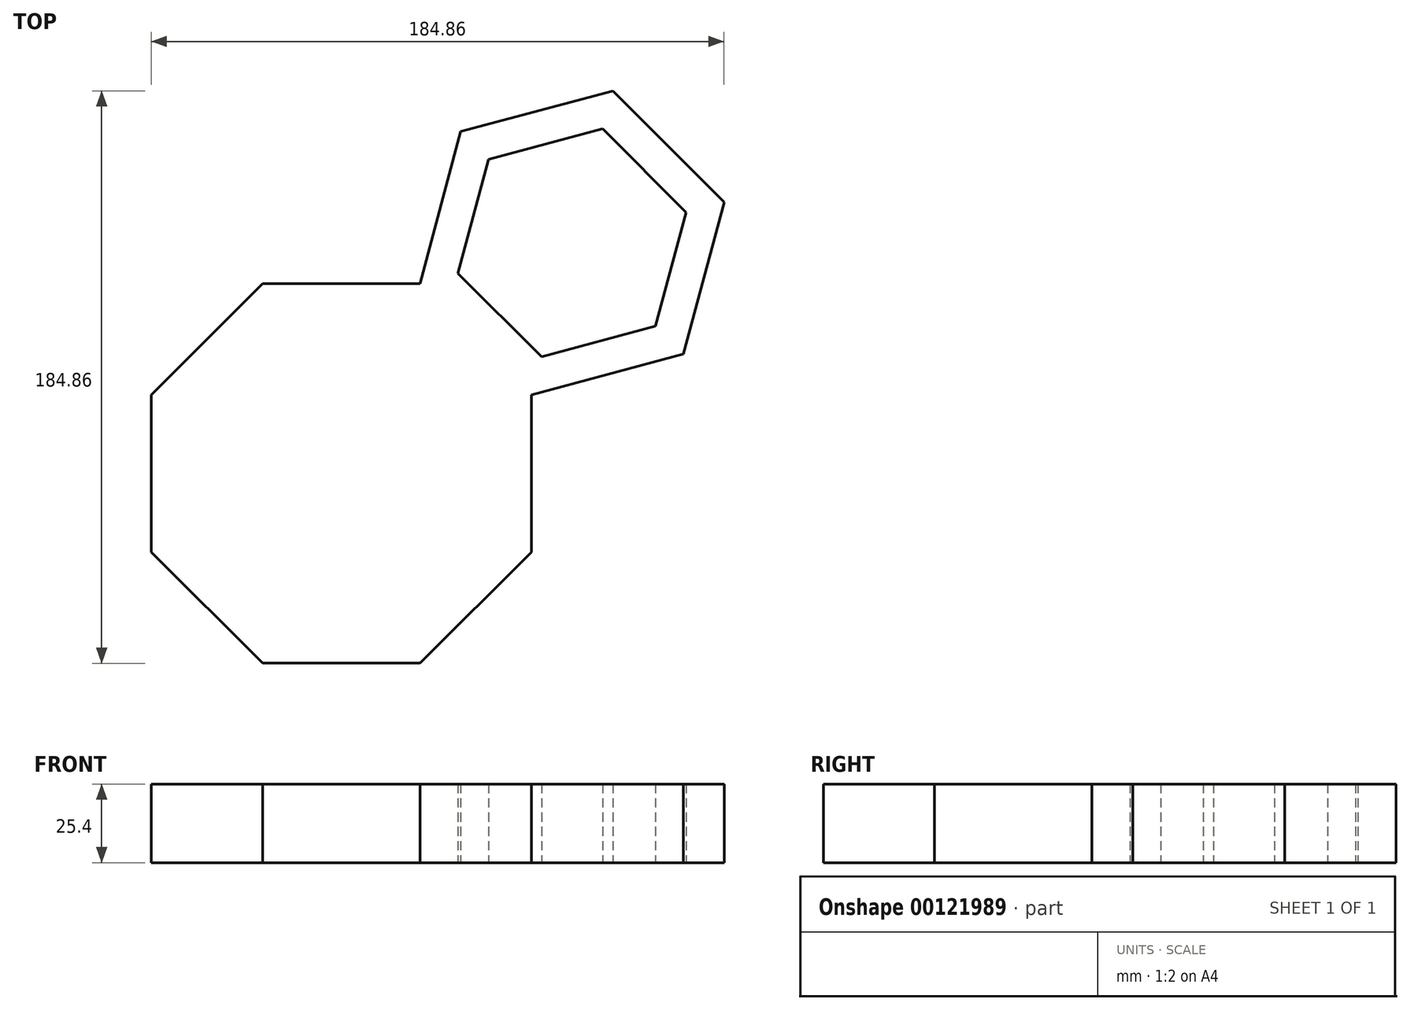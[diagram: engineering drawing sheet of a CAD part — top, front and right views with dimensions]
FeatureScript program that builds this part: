
annotation { "Feature Type Name" : "Feature", "Feature Type Description" : "" }
export const myFeature = defineFeature(function(context is Context, id is Id, definition is map)
    precondition{}
    {
        {
            var Q0;
            Q0=qCreatedBy(makeId("Top.planeOp"),FACE);
            var sketch = newSketch(context, id + "F0", { "sketchPlane" : qUnion([Q0])});
            skCircle(sketch, "E0.cCircle", {"center": v(-1.9, -3.87) * mm, "radius": 61.32 * mm, "construction": true});
            skLineSegment(sketch, "E0.0", {"start": v(59.43, 21.53) * mm, "end": v(59.43, -29.27) * mm});
            skLineSegment(sketch, "E0.1", {"start": v(59.43, -29.27) * mm, "end": v(23.5, -65.2) * mm});
            skLineSegment(sketch, "E0.2", {"start": v(23.5, -65.2) * mm, "end": v(-27.3, -65.2) * mm});
            skLineSegment(sketch, "E0.3", {"start": v(-27.3, -65.2) * mm, "end": v(-63.22, -29.27) * mm});
            skLineSegment(sketch, "E0.4", {"start": v(-63.22, -29.27) * mm, "end": v(-63.22, 21.53) * mm});
            skLineSegment(sketch, "E0.5", {"start": v(-63.22, 21.53) * mm, "end": v(-27.3, 57.45) * mm});
            skLineSegment(sketch, "E0.6", {"start": v(-27.3, 57.45) * mm, "end": v(23.5, 57.45) * mm});
            skLineSegment(sketch, "E0.7", {"start": v(23.5, 57.45) * mm, "end": v(59.43, 21.53) * mm});
            skPoint(sketch, "E0.0.midPoint", {"position": v(59.43, -3.87) * mm});
            skPoint(sketch, "E1.0.midPoint", {"position": v(19.57, 48.7) * mm});
            skCircle(sketch, "E2.cCircle", {"center": v(72.57, 70.6) * mm, "radius": 44 * mm, "construction": true});
            skLineSegment(sketch, "E2.0", {"start": v(36.65, 106.52) * mm, "end": v(85.72, 119.66) * mm});
            skLineSegment(sketch, "E2.1", {"start": v(85.72, 119.66) * mm, "end": v(121.64, 83.74) * mm});
            skLineSegment(sketch, "E2.2", {"start": v(121.64, 83.74) * mm, "end": v(108.5, 34.67) * mm});
            skLineSegment(sketch, "E2.3", {"start": v(108.5, 34.67) * mm, "end": v(59.43, 21.53) * mm});
            skLineSegment(sketch, "E2.4", {"start": v(59.43, 21.53) * mm, "end": v(23.5, 57.45) * mm});
            skLineSegment(sketch, "E2.5", {"start": v(23.5, 57.45) * mm, "end": v(36.65, 106.52) * mm});
            skPoint(sketch, "E2.0.midPoint", {"position": v(61.19, 113.09) * mm});
            skCircle(sketch, "E3.cCircle", {"center": v(72.57, 70.6) * mm, "radius": 33 * mm, "construction": true});
            skLineSegment(sketch, "E3.0", {"start": v(82.43, 107.4) * mm, "end": v(109.38, 80.46) * mm});
            skLineSegment(sketch, "E3.1", {"start": v(109.38, 80.46) * mm, "end": v(99.51, 43.65) * mm});
            skLineSegment(sketch, "E3.2", {"start": v(99.51, 43.65) * mm, "end": v(62.71, 33.8) * mm});
            skLineSegment(sketch, "E3.3", {"start": v(62.71, 33.8) * mm, "end": v(35.77, 60.73) * mm});
            skLineSegment(sketch, "E3.4", {"start": v(35.77, 60.73) * mm, "end": v(45.63, 97.54) * mm});
            skLineSegment(sketch, "E3.5", {"start": v(45.63, 97.54) * mm, "end": v(82.43, 107.4) * mm});
            skPoint(sketch, "E3.0.midPoint", {"position": v(95.9, 93.93) * mm});
            skCircle(sketch, "E4.cCircle", {"center": v(-76.36, 70.6) * mm, "radius": 44 * mm, "construction": true});
            skLineSegment(sketch, "E4.0", {"start": v(-27.3, 57.45) * mm, "end": v(-63.22, 21.53) * mm});
            skLineSegment(sketch, "E4.1", {"start": v(-63.22, 21.53) * mm, "end": v(-112.29, 34.67) * mm});
            skLineSegment(sketch, "E4.2", {"start": v(-112.29, 34.67) * mm, "end": v(-125.43, 83.74) * mm});
            skLineSegment(sketch, "E4.3", {"start": v(-125.43, 83.74) * mm, "end": v(-89.51, 119.66) * mm});
            skLineSegment(sketch, "E4.4", {"start": v(-89.51, 119.66) * mm, "end": v(-40.44, 106.52) * mm});
            skLineSegment(sketch, "E4.5", {"start": v(-40.44, 106.52) * mm, "end": v(-27.3, 57.45) * mm});
            skPoint(sketch, "E4.0.midPoint", {"position": v(-45.26, 39.49) * mm});
            skCircle(sketch, "E5.cCircle", {"center": v(-76.36, 70.6) * mm, "radius": 33 * mm, "construction": true});
            skLineSegment(sketch, "E5.0", {"start": v(-49.42, 97.54) * mm, "end": v(-39.56, 60.73) * mm});
            skLineSegment(sketch, "E5.1", {"start": v(-39.56, 60.73) * mm, "end": v(-66.5, 33.8) * mm});
            skLineSegment(sketch, "E5.2", {"start": v(-66.5, 33.8) * mm, "end": v(-103.3, 43.65) * mm});
            skLineSegment(sketch, "E5.3", {"start": v(-103.3, 43.65) * mm, "end": v(-113.17, 80.46) * mm});
            skLineSegment(sketch, "E5.4", {"start": v(-113.17, 80.46) * mm, "end": v(-86.23, 107.4) * mm});
            skLineSegment(sketch, "E5.5", {"start": v(-86.23, 107.4) * mm, "end": v(-49.42, 97.54) * mm});
            skPoint(sketch, "E5.0.midPoint", {"position": v(-44.5, 79.13) * mm});
            skCircle(sketch, "E6.cCircle", {"center": v(72.57, -78.34) * mm, "radius": 44 * mm, "construction": true});
            skLineSegment(sketch, "E6.0", {"start": v(23.5, -65.2) * mm, "end": v(59.43, -29.27) * mm});
            skLineSegment(sketch, "E6.1", {"start": v(59.43, -29.27) * mm, "end": v(108.5, -42.42) * mm});
            skLineSegment(sketch, "E6.2", {"start": v(108.5, -42.42) * mm, "end": v(121.64, -91.5) * mm});
            skLineSegment(sketch, "E6.3", {"start": v(121.64, -91.5) * mm, "end": v(85.72, -127.41) * mm});
            skLineSegment(sketch, "E6.4", {"start": v(85.72, -127.41) * mm, "end": v(36.65, -114.26) * mm});
            skLineSegment(sketch, "E6.5", {"start": v(36.65, -114.26) * mm, "end": v(23.5, -65.2) * mm});
            skPoint(sketch, "E6.0.midPoint", {"position": v(41.47, -47.23) * mm});
            skCircle(sketch, "E7.cCircle", {"center": v(72.57, -78.34) * mm, "radius": 33 * mm, "construction": true});
            skLineSegment(sketch, "E7.0", {"start": v(62.71, -41.54) * mm, "end": v(99.51, -51.4) * mm});
            skLineSegment(sketch, "E7.1", {"start": v(99.51, -51.4) * mm, "end": v(109.38, -88.2) * mm});
            skLineSegment(sketch, "E7.2", {"start": v(109.38, -88.2) * mm, "end": v(82.43, -115.15) * mm});
            skLineSegment(sketch, "E7.3", {"start": v(82.43, -115.15) * mm, "end": v(45.63, -105.28) * mm});
            skLineSegment(sketch, "E7.4", {"start": v(45.63, -105.28) * mm, "end": v(35.77, -68.48) * mm});
            skLineSegment(sketch, "E7.5", {"start": v(35.77, -68.48) * mm, "end": v(62.71, -41.54) * mm});
            skPoint(sketch, "E7.0.midPoint", {"position": v(81.11, -46.47) * mm});
            skCircle(sketch, "E8.cCircle", {"center": v(-76.36, -78.34) * mm, "radius": 44 * mm, "construction": true});
            skLineSegment(sketch, "E8.0", {"start": v(-63.22, -29.27) * mm, "end": v(-27.3, -65.2) * mm});
            skLineSegment(sketch, "E8.1", {"start": v(-27.3, -65.2) * mm, "end": v(-40.44, -114.26) * mm});
            skLineSegment(sketch, "E8.2", {"start": v(-40.44, -114.26) * mm, "end": v(-89.51, -127.41) * mm});
            skLineSegment(sketch, "E8.3", {"start": v(-89.51, -127.41) * mm, "end": v(-125.43, -91.5) * mm});
            skLineSegment(sketch, "E8.4", {"start": v(-125.43, -91.5) * mm, "end": v(-112.29, -42.42) * mm});
            skLineSegment(sketch, "E8.5", {"start": v(-112.29, -42.42) * mm, "end": v(-63.22, -29.27) * mm});
            skPoint(sketch, "E8.0.midPoint", {"position": v(-45.26, -47.23) * mm});
            skCircle(sketch, "E9.cCircle", {"center": v(-76.36, -78.34) * mm, "radius": 33 * mm, "construction": true});
            skLineSegment(sketch, "E9.0", {"start": v(-103.3, -51.4) * mm, "end": v(-66.5, -41.54) * mm});
            skLineSegment(sketch, "E9.1", {"start": v(-66.5, -41.54) * mm, "end": v(-39.56, -68.48) * mm});
            skLineSegment(sketch, "E9.2", {"start": v(-39.56, -68.48) * mm, "end": v(-49.42, -105.28) * mm});
            skLineSegment(sketch, "E9.3", {"start": v(-49.42, -105.28) * mm, "end": v(-86.23, -115.15) * mm});
            skLineSegment(sketch, "E9.4", {"start": v(-86.23, -115.15) * mm, "end": v(-113.17, -88.2) * mm});
            skLineSegment(sketch, "E9.5", {"start": v(-113.17, -88.2) * mm, "end": v(-103.3, -51.4) * mm});
            skPoint(sketch, "E9.0.midPoint", {"position": v(-84.9, -46.47) * mm});
            skSolve(sketch);
        }
        {
            var Q0;
            Q0=makeQuery(id+"F0.imprint","IMPRINT",FACE,{"disambiguationData":[TD([[makeQuery(id+"F0.imprint","IMPRINT",EDGE,{"derivedFrom":sQuery(id+"F0.wireOp",EDGE,"E4.0")}),-1.0]])]});
            var Q1;
            Q1=makeQuery(id+"F0.imprint","IMPRINT",FACE,{"disambiguationData":[TD([[makeQuery(id+"F0.imprint","IMPRINT",EDGE,{"derivedFrom":sQuery(id+"F0.wireOp",EDGE,"E0.0")}),-1.0]])]});
            var Q2;
            Q2=makeQuery(id+"F0.imprint","IMPRINT",FACE,{"disambiguationData":[TD([[makeQuery(id+"F0.imprint","IMPRINT",EDGE,{"derivedFrom":sQuery(id+"F0.wireOp",EDGE,"E8.0")}),-1.0]])]});
            var Q3;
            Q3=makeQuery(id+"F0.imprint","IMPRINT",FACE,{"disambiguationData":[TD([[makeQuery(id+"F0.imprint","IMPRINT",EDGE,{"derivedFrom":sQuery(id+"F0.wireOp",EDGE,"E6.0")}),-1.0]])]});
            var Q4;
            Q4=makeQuery(id+"F0.imprint","IMPRINT",FACE,{"disambiguationData":[TD([[makeQuery(id+"F0.imprint","IMPRINT",EDGE,{"derivedFrom":sQuery(id+"F0.wireOp",EDGE,"E2.0")}),-1.0]])]});
            extrude(context, id + "F1", {"entities" : qUnion([Q0, Q1, Q2, Q3, Q4]), "depth" : 25.4 * mm});
        }
    });
